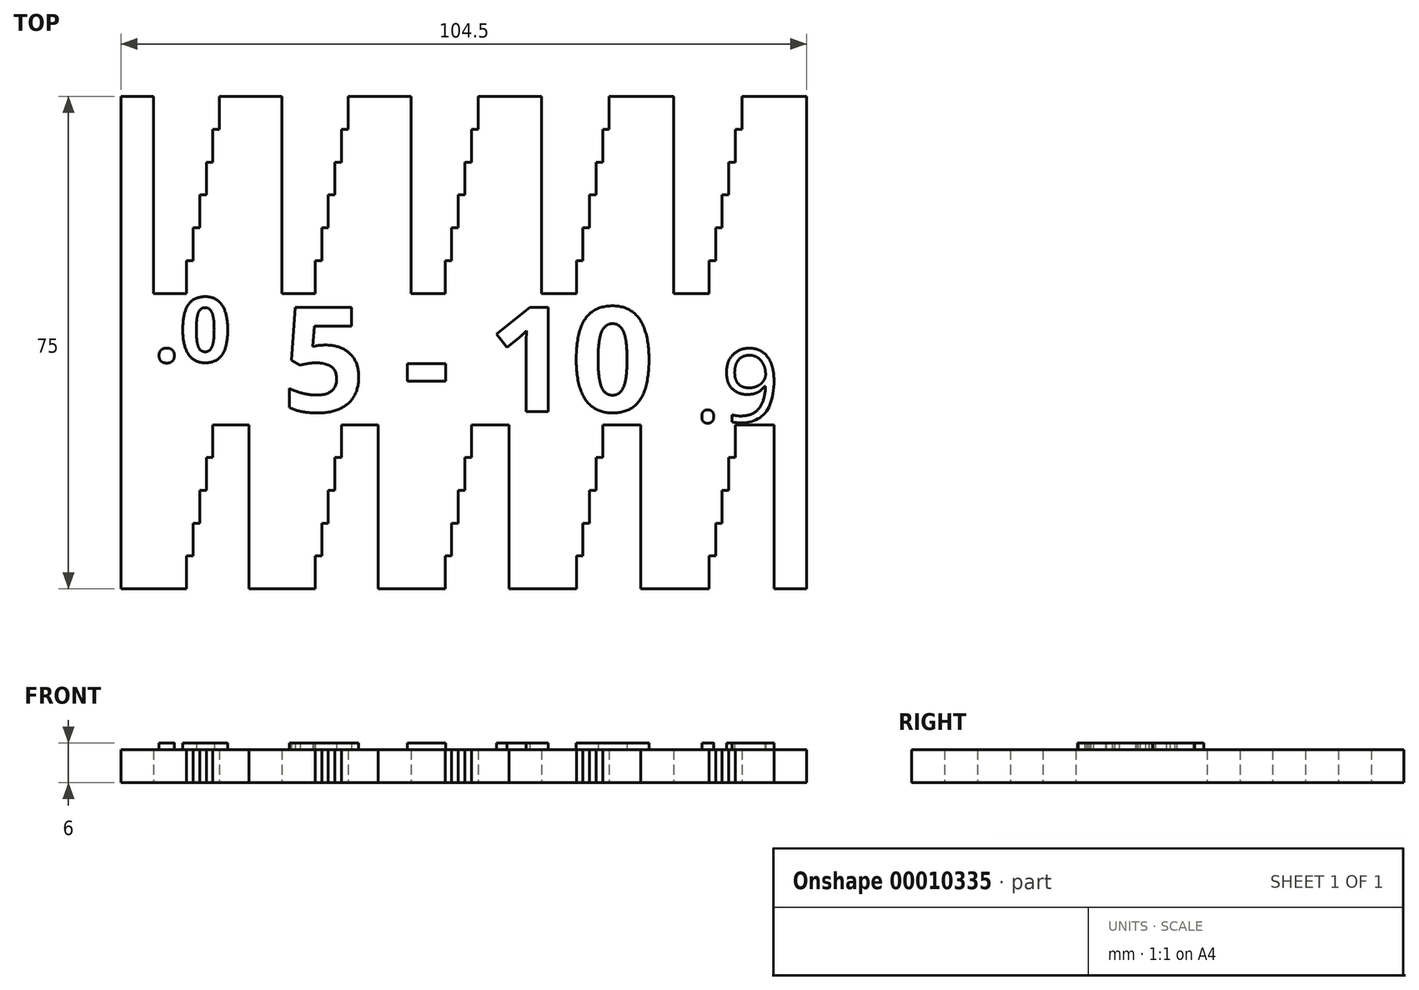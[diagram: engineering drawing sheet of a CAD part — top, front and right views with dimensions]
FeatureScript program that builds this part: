
annotation { "Feature Type Name" : "Feature", "Feature Type Description" : "" }
export const myFeature = defineFeature(function(context is Context, id is Id, definition is map)
    precondition{}
    {
        {
            var Q0;
            Q0=qCreatedBy(makeId("Top.planeOp"),FACE);
            var sketch = newSketch(context, id + "F0", { "sketchPlane" : qUnion([Q0])});
            skLineSegment(sketch, "E0.bottom", {"start": v(-54.67, 33.99) * mm, "end": v(49.83, 33.99) * mm, "construction": true});
            skLineSegment(sketch, "E0.top", {"start": v(-54.67, -41.01) * mm, "end": v(49.83, -41.01) * mm, "construction": true});
            skLineSegment(sketch, "E0.left", {"start": v(-54.67, 33.99) * mm, "end": v(-54.67, -41.01) * mm, "construction": true});
            skLineSegment(sketch, "E0.right", {"start": v(49.83, 33.99) * mm, "end": v(49.83, -41.01) * mm, "construction": true});
            skLineSegment(sketch, "E1.bottom", {"start": v(-54.67, 33.99) * mm, "end": v(-49.67, 33.99) * mm});
            skLineSegment(sketch, "E1.top", {"start": v(-54.67, -41.01) * mm, "end": v(-49.67, -41.01) * mm});
            skLineSegment(sketch, "E1.left", {"start": v(-54.67, 33.99) * mm, "end": v(-54.67, -41.01) * mm});
            skLineSegment(sketch, "E1.right", {"start": v(-49.67, 33.99) * mm, "end": v(-49.67, -41.01) * mm});
            skLineSegment(sketch, "E2.bottom", {"start": v(-49.67, 3.99) * mm, "end": v(-44.67, 3.99) * mm});
            skLineSegment(sketch, "E2.top", {"start": v(-49.67, -41.01) * mm, "end": v(-44.67, -41.01) * mm});
            skLineSegment(sketch, "E2.left", {"start": v(-49.67, 3.99) * mm, "end": v(-49.67, -41.01) * mm});
            skLineSegment(sketch, "E2.right", {"start": v(-44.67, 3.99) * mm, "end": v(-44.67, -41.01) * mm});
            skLineSegment(sketch, "E3.bottom", {"start": v(-44.67, -36.01) * mm, "end": v(-43.67, -36.01) * mm});
            skLineSegment(sketch, "E3.top", {"start": v(-44.67, 8.99) * mm, "end": v(-43.67, 8.99) * mm});
            skLineSegment(sketch, "E3.left", {"start": v(-44.67, -36.01) * mm, "end": v(-44.67, 8.99) * mm});
            skLineSegment(sketch, "E3.right", {"start": v(-43.67, -36.01) * mm, "end": v(-43.67, 8.99) * mm});
            skLineSegment(sketch, "E4.bottom", {"start": v(-43.67, -31.01) * mm, "end": v(-42.67, -31.01) * mm});
            skLineSegment(sketch, "E4.top", {"start": v(-43.67, 13.99) * mm, "end": v(-42.67, 13.99) * mm});
            skLineSegment(sketch, "E4.left", {"start": v(-43.67, -31.01) * mm, "end": v(-43.67, 13.99) * mm});
            skLineSegment(sketch, "E4.right", {"start": v(-42.67, -31.01) * mm, "end": v(-42.67, 13.99) * mm});
            skLineSegment(sketch, "E5.bottom", {"start": v(-42.67, -26.01) * mm, "end": v(-41.67, -26.01) * mm});
            skLineSegment(sketch, "E5.top", {"start": v(-42.67, 18.99) * mm, "end": v(-41.67, 18.99) * mm});
            skLineSegment(sketch, "E5.left", {"start": v(-42.67, -26.01) * mm, "end": v(-42.67, 18.99) * mm});
            skLineSegment(sketch, "E5.right", {"start": v(-41.67, -26.01) * mm, "end": v(-41.67, 18.99) * mm});
            skLineSegment(sketch, "E6.bottom", {"start": v(-41.67, -21.01) * mm, "end": v(-40.67, -21.01) * mm});
            skLineSegment(sketch, "E6.top", {"start": v(-41.67, 23.99) * mm, "end": v(-40.67, 23.99) * mm});
            skLineSegment(sketch, "E6.left", {"start": v(-41.67, -21.01) * mm, "end": v(-41.67, 23.99) * mm});
            skLineSegment(sketch, "E6.right", {"start": v(-40.67, -21.01) * mm, "end": v(-40.67, 23.99) * mm});
            skLineSegment(sketch, "E7.bottom", {"start": v(-40.67, -16.01) * mm, "end": v(-39.67, -16.01) * mm});
            skLineSegment(sketch, "E7.top", {"start": v(-40.67, 28.99) * mm, "end": v(-39.67, 28.99) * mm});
            skLineSegment(sketch, "E7.left", {"start": v(-40.67, -16.01) * mm, "end": v(-40.67, 28.99) * mm});
            skLineSegment(sketch, "E7.right", {"start": v(-39.67, -16.01) * mm, "end": v(-39.67, 28.99) * mm});
            skLineSegment(sketch, "E8.bottom", {"start": v(-39.67, -16.01) * mm, "end": v(-35.17, -16.01) * mm});
            skLineSegment(sketch, "E8.top", {"start": v(-39.67, 33.99) * mm, "end": v(-35.17, 33.99) * mm});
            skLineSegment(sketch, "E8.left", {"start": v(-39.67, -16.01) * mm, "end": v(-39.67, 33.99) * mm});
            skLineSegment(sketch, "E8.right", {"start": v(-35.17, -16.01) * mm, "end": v(-35.17, 33.99) * mm});
            skLineSegment(sketch, "E9.right", {"start": v(-22.07, -26.01) * mm, "end": v(-22.07, 18.99) * mm});
            skLineSegment(sketch, "E10.right", {"start": v(-20.07, -16.01) * mm, "end": v(-20.07, 28.99) * mm});
            skLineSegment(sketch, "E11.left", {"start": v(-20.07, -16.01) * mm, "end": v(-20.07, 33.99) * mm});
            skLineSegment(sketch, "E12.left", {"start": v(-30.17, 3.99) * mm, "end": v(-30.17, -41.01) * mm});
            skLineSegment(sketch, "E12.right", {"start": v(-25.07, 3.99) * mm, "end": v(-25.07, -41.01) * mm});
            skLineSegment(sketch, "E13.right", {"start": v(-21.07, -21.01) * mm, "end": v(-21.07, 23.99) * mm});
            skLineSegment(sketch, "E11.right", {"start": v(-15.47, -16.01) * mm, "end": v(-15.47, 33.99) * mm});
            skLineSegment(sketch, "E14.right", {"start": v(-23.07, -31.01) * mm, "end": v(-23.07, 13.99) * mm});
            skLineSegment(sketch, "E13.left", {"start": v(-22.07, -21.01) * mm, "end": v(-22.07, 23.99) * mm});
            skLineSegment(sketch, "E11.bottom", {"start": v(-20.07, -16.01) * mm, "end": v(-15.47, -16.01) * mm});
            skLineSegment(sketch, "E9.left", {"start": v(-23.07, -26.01) * mm, "end": v(-23.07, 18.99) * mm});
            skLineSegment(sketch, "E10.left", {"start": v(-21.07, -16.01) * mm, "end": v(-21.07, 28.99) * mm});
            skLineSegment(sketch, "E15.bottom", {"start": v(-35.17, 33.99) * mm, "end": v(-30.17, 33.99) * mm});
            skLineSegment(sketch, "E15.left", {"start": v(-35.17, 33.99) * mm, "end": v(-35.17, -41.01) * mm});
            skLineSegment(sketch, "E15.top", {"start": v(-35.17, -41.01) * mm, "end": v(-30.17, -41.01) * mm});
            skLineSegment(sketch, "E12.bottom", {"start": v(-30.17, 3.99) * mm, "end": v(-25.07, 3.99) * mm});
            skLineSegment(sketch, "E15.right", {"start": v(-30.17, 33.99) * mm, "end": v(-30.17, -41.01) * mm});
            skLineSegment(sketch, "E12.top", {"start": v(-30.17, -41.01) * mm, "end": v(-25.07, -41.01) * mm});
            skLineSegment(sketch, "E16.left", {"start": v(-25.07, -36.01) * mm, "end": v(-25.07, 8.99) * mm});
            skLineSegment(sketch, "E14.left", {"start": v(-24.07, -31.01) * mm, "end": v(-24.07, 13.99) * mm});
            skLineSegment(sketch, "E16.right", {"start": v(-24.07, -36.01) * mm, "end": v(-24.07, 8.99) * mm});
            skLineSegment(sketch, "E11.top", {"start": v(-20.07, 33.99) * mm, "end": v(-15.47, 33.99) * mm});
            skLineSegment(sketch, "E16.top", {"start": v(-25.07, 8.99) * mm, "end": v(-24.07, 8.99) * mm});
            skLineSegment(sketch, "E14.bottom", {"start": v(-24.07, -31.01) * mm, "end": v(-23.07, -31.01) * mm});
            skLineSegment(sketch, "E10.bottom", {"start": v(-21.07, -16.01) * mm, "end": v(-20.07, -16.01) * mm});
            skLineSegment(sketch, "E13.top", {"start": v(-22.07, 23.99) * mm, "end": v(-21.07, 23.99) * mm});
            skLineSegment(sketch, "E17.left", {"start": v(-35.59, 33.94) * mm, "end": v(-35.59, -41.06) * mm, "construction": true});
            skLineSegment(sketch, "E14.top", {"start": v(-24.07, 13.99) * mm, "end": v(-23.07, 13.99) * mm});
            skLineSegment(sketch, "E9.top", {"start": v(-23.07, 18.99) * mm, "end": v(-22.07, 18.99) * mm});
            skLineSegment(sketch, "E9.bottom", {"start": v(-23.07, -26.01) * mm, "end": v(-22.07, -26.01) * mm});
            skLineSegment(sketch, "E10.top", {"start": v(-21.07, 28.99) * mm, "end": v(-20.07, 28.99) * mm});
            skLineSegment(sketch, "E16.bottom", {"start": v(-25.07, -36.01) * mm, "end": v(-24.07, -36.01) * mm});
            skLineSegment(sketch, "E13.bottom", {"start": v(-22.07, -21.01) * mm, "end": v(-21.07, -21.01) * mm});
            skLineSegment(sketch, "E18.right", {"start": v(-2.27, -26.01) * mm, "end": v(-2.27, 18.99) * mm});
            skLineSegment(sketch, "E19.right", {"start": v(-0.27, -16.01) * mm, "end": v(-0.27, 28.99) * mm});
            skLineSegment(sketch, "E20.left", {"start": v(-0.27, -16.01) * mm, "end": v(-0.27, 33.99) * mm});
            skLineSegment(sketch, "E21.left", {"start": v(-10.47, 3.99) * mm, "end": v(-10.47, -41.01) * mm});
            skLineSegment(sketch, "E21.right", {"start": v(-5.27, 3.99) * mm, "end": v(-5.27, -41.01) * mm});
            skLineSegment(sketch, "E22.right", {"start": v(-1.27, -21.01) * mm, "end": v(-1.27, 23.99) * mm});
            skLineSegment(sketch, "E20.right", {"start": v(4.43, -16.01) * mm, "end": v(4.43, 33.99) * mm});
            skLineSegment(sketch, "E23.right", {"start": v(-3.27, -31.01) * mm, "end": v(-3.27, 13.99) * mm});
            skLineSegment(sketch, "E22.left", {"start": v(-2.27, -21.01) * mm, "end": v(-2.27, 23.99) * mm});
            skLineSegment(sketch, "E20.bottom", {"start": v(-0.27, -16.01) * mm, "end": v(4.43, -16.01) * mm});
            skLineSegment(sketch, "E18.left", {"start": v(-3.27, -26.01) * mm, "end": v(-3.27, 18.99) * mm});
            skLineSegment(sketch, "E19.left", {"start": v(-1.27, -16.01) * mm, "end": v(-1.27, 28.99) * mm});
            skLineSegment(sketch, "E24.bottom", {"start": v(-15.47, 33.99) * mm, "end": v(-10.47, 33.99) * mm});
            skLineSegment(sketch, "E24.left", {"start": v(-15.47, 33.99) * mm, "end": v(-15.47, -41.01) * mm});
            skLineSegment(sketch, "E24.top", {"start": v(-15.47, -41.01) * mm, "end": v(-10.47, -41.01) * mm});
            skLineSegment(sketch, "E21.bottom", {"start": v(-10.47, 3.99) * mm, "end": v(-5.27, 3.99) * mm});
            skLineSegment(sketch, "E24.right", {"start": v(-10.47, 33.99) * mm, "end": v(-10.47, -41.01) * mm});
            skLineSegment(sketch, "E21.top", {"start": v(-10.47, -41.01) * mm, "end": v(-5.27, -41.01) * mm});
            skLineSegment(sketch, "E25.left", {"start": v(-5.27, -36.01) * mm, "end": v(-5.27, 8.99) * mm});
            skLineSegment(sketch, "E23.left", {"start": v(-4.27, -31.01) * mm, "end": v(-4.27, 13.99) * mm});
            skLineSegment(sketch, "E25.right", {"start": v(-4.27, -36.01) * mm, "end": v(-4.27, 8.99) * mm});
            skLineSegment(sketch, "E20.top", {"start": v(-0.27, 33.99) * mm, "end": v(4.43, 33.99) * mm});
            skLineSegment(sketch, "E25.top", {"start": v(-5.27, 8.99) * mm, "end": v(-4.27, 8.99) * mm});
            skLineSegment(sketch, "E23.bottom", {"start": v(-4.27, -31.01) * mm, "end": v(-3.27, -31.01) * mm});
            skLineSegment(sketch, "E19.bottom", {"start": v(-1.27, -16.01) * mm, "end": v(-0.27, -16.01) * mm});
            skLineSegment(sketch, "E22.top", {"start": v(-2.27, 23.99) * mm, "end": v(-1.27, 23.99) * mm});
            skLineSegment(sketch, "E23.top", {"start": v(-4.27, 13.99) * mm, "end": v(-3.27, 13.99) * mm});
            skLineSegment(sketch, "E18.top", {"start": v(-3.27, 18.99) * mm, "end": v(-2.27, 18.99) * mm});
            skLineSegment(sketch, "E18.bottom", {"start": v(-3.27, -26.01) * mm, "end": v(-2.27, -26.01) * mm});
            skLineSegment(sketch, "E19.top", {"start": v(-1.27, 28.99) * mm, "end": v(-0.27, 28.99) * mm});
            skLineSegment(sketch, "E25.bottom", {"start": v(-5.27, -36.01) * mm, "end": v(-4.27, -36.01) * mm});
            skLineSegment(sketch, "E22.bottom", {"start": v(-2.27, -21.01) * mm, "end": v(-1.27, -21.01) * mm});
            skLineSegment(sketch, "E26.left", {"start": v(15.73, -31.01) * mm, "end": v(15.73, 13.99) * mm});
            skLineSegment(sketch, "E27.right", {"start": v(37.93, -26.01) * mm, "end": v(37.93, 18.99) * mm});
            skLineSegment(sketch, "E28.right", {"start": v(35.93, -36.01) * mm, "end": v(35.93, 8.99) * mm});
            skLineSegment(sketch, "E29.bottom", {"start": v(19.73, -16.01) * mm, "end": v(24.53, -16.01) * mm});
            skLineSegment(sketch, "E30.bottom", {"start": v(24.53, 33.99) * mm, "end": v(29.53, 33.99) * mm});
            skLineSegment(sketch, "E30.right", {"start": v(29.53, 33.99) * mm, "end": v(29.53, -41.01) * mm});
            skLineSegment(sketch, "E31.right", {"start": v(34.93, 3.99) * mm, "end": v(34.93, -41.01) * mm});
            skLineSegment(sketch, "E32.right", {"start": v(49.83, 33.99) * mm, "end": v(49.83, -41.01) * mm});
            skLineSegment(sketch, "E33.left", {"start": v(39.93, -16.01) * mm, "end": v(39.93, 33.99) * mm});
            skLineSegment(sketch, "E33.top", {"start": v(39.93, 33.99) * mm, "end": v(44.83, 33.99) * mm});
            skLineSegment(sketch, "E28.left", {"start": v(34.93, -36.01) * mm, "end": v(34.93, 8.99) * mm});
            skLineSegment(sketch, "E34.right", {"start": v(38.93, -21.01) * mm, "end": v(38.93, 23.99) * mm});
            skLineSegment(sketch, "E35.left", {"start": v(16.73, -26.01) * mm, "end": v(16.73, 18.99) * mm});
            skLineSegment(sketch, "E36.top", {"start": v(38.93, 28.99) * mm, "end": v(39.93, 28.99) * mm});
            skLineSegment(sketch, "E31.left", {"start": v(29.53, 3.99) * mm, "end": v(29.53, -41.01) * mm});
            skLineSegment(sketch, "E35.right", {"start": v(17.73, -26.01) * mm, "end": v(17.73, 18.99) * mm});
            skLineSegment(sketch, "E32.left", {"start": v(44.83, 33.99) * mm, "end": v(44.83, -41.01) * mm});
            skLineSegment(sketch, "E29.left", {"start": v(19.73, -16.01) * mm, "end": v(19.73, 33.99) * mm});
            skLineSegment(sketch, "E37.right", {"start": v(14.73, 3.99) * mm, "end": v(14.73, -41.01) * mm});
            skLineSegment(sketch, "E38.left", {"start": v(35.93, -31.01) * mm, "end": v(35.93, 13.99) * mm});
            skLineSegment(sketch, "E39.bottom", {"start": v(17.73, -21.01) * mm, "end": v(18.73, -21.01) * mm});
            skLineSegment(sketch, "E40.top", {"start": v(18.73, 28.99) * mm, "end": v(19.73, 28.99) * mm});
            skLineSegment(sketch, "E33.bottom", {"start": v(39.93, -16.01) * mm, "end": v(44.83, -16.01) * mm});
            skLineSegment(sketch, "E30.top", {"start": v(24.53, -41.01) * mm, "end": v(29.53, -41.01) * mm});
            skLineSegment(sketch, "E39.left", {"start": v(17.73, -21.01) * mm, "end": v(17.73, 23.99) * mm});
            skLineSegment(sketch, "E28.top", {"start": v(34.93, 8.99) * mm, "end": v(35.93, 8.99) * mm});
            skLineSegment(sketch, "E40.left", {"start": v(18.73, -16.01) * mm, "end": v(18.73, 28.99) * mm});
            skLineSegment(sketch, "E33.right", {"start": v(44.83, -16.01) * mm, "end": v(44.83, 33.99) * mm});
            skLineSegment(sketch, "E27.left", {"start": v(36.93, -26.01) * mm, "end": v(36.93, 18.99) * mm});
            skLineSegment(sketch, "E41.right", {"start": v(15.73, -36.01) * mm, "end": v(15.73, 8.99) * mm});
            skLineSegment(sketch, "E31.top", {"start": v(29.53, -41.01) * mm, "end": v(34.93, -41.01) * mm});
            skLineSegment(sketch, "E36.right", {"start": v(39.93, -16.01) * mm, "end": v(39.93, 28.99) * mm});
            skLineSegment(sketch, "E41.left", {"start": v(14.73, -36.01) * mm, "end": v(14.73, 8.99) * mm});
            skLineSegment(sketch, "E34.left", {"start": v(37.93, -21.01) * mm, "end": v(37.93, 23.99) * mm});
            skLineSegment(sketch, "E40.right", {"start": v(19.73, -16.01) * mm, "end": v(19.73, 28.99) * mm});
            skLineSegment(sketch, "E36.left", {"start": v(38.93, -16.01) * mm, "end": v(38.93, 28.99) * mm});
            skLineSegment(sketch, "E39.right", {"start": v(18.73, -21.01) * mm, "end": v(18.73, 23.99) * mm});
            skLineSegment(sketch, "E38.right", {"start": v(36.93, -31.01) * mm, "end": v(36.93, 13.99) * mm});
            skLineSegment(sketch, "E26.right", {"start": v(16.73, -31.01) * mm, "end": v(16.73, 13.99) * mm});
            skLineSegment(sketch, "E29.right", {"start": v(24.53, -16.01) * mm, "end": v(24.53, 33.99) * mm});
            skLineSegment(sketch, "E32.top", {"start": v(44.83, -41.01) * mm, "end": v(49.83, -41.01) * mm});
            skLineSegment(sketch, "E31.bottom", {"start": v(29.53, 3.99) * mm, "end": v(34.93, 3.99) * mm});
            skLineSegment(sketch, "E42.bottom", {"start": v(4.43, 33.99) * mm, "end": v(9.43, 33.99) * mm});
            skLineSegment(sketch, "E42.left", {"start": v(4.43, 33.99) * mm, "end": v(4.43, -41.01) * mm});
            skLineSegment(sketch, "E42.top", {"start": v(4.43, -41.01) * mm, "end": v(9.43, -41.01) * mm});
            skLineSegment(sketch, "E37.bottom", {"start": v(9.43, 3.99) * mm, "end": v(14.73, 3.99) * mm});
            skLineSegment(sketch, "E42.right", {"start": v(9.43, 33.99) * mm, "end": v(9.43, -41.01) * mm});
            skLineSegment(sketch, "E37.left", {"start": v(9.43, 3.99) * mm, "end": v(9.43, -41.01) * mm});
            skLineSegment(sketch, "E29.top", {"start": v(19.73, 33.99) * mm, "end": v(24.53, 33.99) * mm});
            skLineSegment(sketch, "E30.left", {"start": v(24.53, 33.99) * mm, "end": v(24.53, -41.01) * mm});
            skLineSegment(sketch, "E34.top", {"start": v(37.93, 23.99) * mm, "end": v(38.93, 23.99) * mm});
            skLineSegment(sketch, "E37.top", {"start": v(9.43, -41.01) * mm, "end": v(14.73, -41.01) * mm});
            skLineSegment(sketch, "E27.bottom", {"start": v(36.93, -26.01) * mm, "end": v(37.93, -26.01) * mm});
            skLineSegment(sketch, "E32.bottom", {"start": v(44.83, 33.99) * mm, "end": v(49.83, 33.99) * mm});
            skLineSegment(sketch, "E41.bottom", {"start": v(14.73, -36.01) * mm, "end": v(15.73, -36.01) * mm});
            skLineSegment(sketch, "E34.bottom", {"start": v(37.93, -21.01) * mm, "end": v(38.93, -21.01) * mm});
            skLineSegment(sketch, "E27.top", {"start": v(36.93, 18.99) * mm, "end": v(37.93, 18.99) * mm});
            skLineSegment(sketch, "E38.top", {"start": v(35.93, 13.99) * mm, "end": v(36.93, 13.99) * mm});
            skLineSegment(sketch, "E39.top", {"start": v(17.73, 23.99) * mm, "end": v(18.73, 23.99) * mm});
            skLineSegment(sketch, "E41.top", {"start": v(14.73, 8.99) * mm, "end": v(15.73, 8.99) * mm});
            skLineSegment(sketch, "E35.top", {"start": v(16.73, 18.99) * mm, "end": v(17.73, 18.99) * mm});
            skLineSegment(sketch, "E26.top", {"start": v(15.73, 13.99) * mm, "end": v(16.73, 13.99) * mm});
            skLineSegment(sketch, "E26.bottom", {"start": v(15.73, -31.01) * mm, "end": v(16.73, -31.01) * mm});
            skLineSegment(sketch, "E35.bottom", {"start": v(16.73, -26.01) * mm, "end": v(17.73, -26.01) * mm});
            skLineSegment(sketch, "E36.bottom", {"start": v(38.93, -16.01) * mm, "end": v(39.93, -16.01) * mm});
            skLineSegment(sketch, "E40.bottom", {"start": v(18.73, -16.01) * mm, "end": v(19.73, -16.01) * mm});
            skLineSegment(sketch, "E38.bottom", {"start": v(35.93, -31.01) * mm, "end": v(36.93, -31.01) * mm});
            skLineSegment(sketch, "E28.bottom", {"start": v(34.93, -36.01) * mm, "end": v(35.93, -36.01) * mm});
            skSolve(sketch);
        }
        {
            var Q0;
            Q0 = qSketchRegion(id + "F0", true);
            extrude(context, id + "F1", {"entities" : qUnion([Q0]), "depth" : 5 * mm});
        }
        {
            var Q0;
            Q0=makeQuery(id+"F1.opExtrude","CAP_FACE",FACE,{"disambiguationData":[OSD([sQuery(id+"F0.wireOp",EDGE,"E1.bottom"),sQuery(id+"F0.wireOp",EDGE,"E1.top"),sQuery(id+"F0.wireOp",EDGE,"E1.left"),sQuery(id+"F0.wireOp",EDGE,"E1.right"),sQuery(id+"F0.wireOp",EDGE,"E2.bottom"),sQuery(id+"F0.wireOp",EDGE,"E2.top"),sQuery(id+"F0.wireOp",EDGE,"E2.right"),sQuery(id+"F0.wireOp",EDGE,"E3.bottom"),sQuery(id+"F0.wireOp",EDGE,"E3.top"),sQuery(id+"F0.wireOp",EDGE,"E3.left"),sQuery(id+"F0.wireOp",EDGE,"E3.right"),sQuery(id+"F0.wireOp",EDGE,"E4.bottom"),sQuery(id+"F0.wireOp",EDGE,"E4.top"),sQuery(id+"F0.wireOp",EDGE,"E4.left"),sQuery(id+"F0.wireOp",EDGE,"E4.right"),sQuery(id+"F0.wireOp",EDGE,"E5.bottom"),sQuery(id+"F0.wireOp",EDGE,"E5.top"),sQuery(id+"F0.wireOp",EDGE,"E5.left"),sQuery(id+"F0.wireOp",EDGE,"E5.right"),sQuery(id+"F0.wireOp",EDGE,"E6.bottom"),sQuery(id+"F0.wireOp",EDGE,"E6.top"),sQuery(id+"F0.wireOp",EDGE,"E6.left"),sQuery(id+"F0.wireOp",EDGE,"E6.right"),sQuery(id+"F0.wireOp",EDGE,"E7.bottom"),sQuery(id+"F0.wireOp",EDGE,"E7.top"),sQuery(id+"F0.wireOp",EDGE,"E7.left"),sQuery(id+"F0.wireOp",EDGE,"E8.bottom"),sQuery(id+"F0.wireOp",EDGE,"E8.top"),sQuery(id+"F0.wireOp",EDGE,"E8.left"),sQuery(id+"F0.wireOp",EDGE,"E9.right"),sQuery(id+"F0.wireOp",EDGE,"E11.left"),sQuery(id+"F0.wireOp",EDGE,"E12.right"),sQuery(id+"F0.wireOp",EDGE,"E13.right"),sQuery(id+"F0.wireOp",EDGE,"E14.right"),sQuery(id+"F0.wireOp",EDGE,"E13.left"),sQuery(id+"F0.wireOp",EDGE,"E11.bottom"),sQuery(id+"F0.wireOp",EDGE,"E9.left"),sQuery(id+"F0.wireOp",EDGE,"E10.left"),sQuery(id+"F0.wireOp",EDGE,"E15.bottom"),sQuery(id+"F0.wireOp",EDGE,"E15.left"),sQuery(id+"F0.wireOp",EDGE,"E15.top"),sQuery(id+"F0.wireOp",EDGE,"E12.bottom"),sQuery(id+"F0.wireOp",EDGE,"E15.right"),sQuery(id+"F0.wireOp",EDGE,"E12.top"),sQuery(id+"F0.wireOp",EDGE,"E16.left"),sQuery(id+"F0.wireOp",EDGE,"E14.left"),sQuery(id+"F0.wireOp",EDGE,"E16.right"),sQuery(id+"F0.wireOp",EDGE,"E11.top"),sQuery(id+"F0.wireOp",EDGE,"E16.top"),sQuery(id+"F0.wireOp",EDGE,"E14.bottom"),sQuery(id+"F0.wireOp",EDGE,"E10.bottom"),sQuery(id+"F0.wireOp",EDGE,"E13.top"),sQuery(id+"F0.wireOp",EDGE,"E14.top"),sQuery(id+"F0.wireOp",EDGE,"E9.top"),sQuery(id+"F0.wireOp",EDGE,"E9.bottom"),sQuery(id+"F0.wireOp",EDGE,"E10.top"),sQuery(id+"F0.wireOp",EDGE,"E16.bottom"),sQuery(id+"F0.wireOp",EDGE,"E13.bottom"),sQuery(id+"F0.wireOp",EDGE,"E18.right"),sQuery(id+"F0.wireOp",EDGE,"E20.left"),sQuery(id+"F0.wireOp",EDGE,"E21.right"),sQuery(id+"F0.wireOp",EDGE,"E22.right"),sQuery(id+"F0.wireOp",EDGE,"E23.right"),sQuery(id+"F0.wireOp",EDGE,"E22.left"),sQuery(id+"F0.wireOp",EDGE,"E20.bottom"),sQuery(id+"F0.wireOp",EDGE,"E18.left"),sQuery(id+"F0.wireOp",EDGE,"E19.left"),sQuery(id+"F0.wireOp",EDGE,"E24.bottom"),sQuery(id+"F0.wireOp",EDGE,"E24.left"),sQuery(id+"F0.wireOp",EDGE,"E24.top"),sQuery(id+"F0.wireOp",EDGE,"E21.bottom"),sQuery(id+"F0.wireOp",EDGE,"E24.right"),sQuery(id+"F0.wireOp",EDGE,"E21.top"),sQuery(id+"F0.wireOp",EDGE,"E25.left"),sQuery(id+"F0.wireOp",EDGE,"E23.left"),sQuery(id+"F0.wireOp",EDGE,"E25.right"),sQuery(id+"F0.wireOp",EDGE,"E20.top"),sQuery(id+"F0.wireOp",EDGE,"E25.top"),sQuery(id+"F0.wireOp",EDGE,"E23.bottom"),sQuery(id+"F0.wireOp",EDGE,"E19.bottom"),sQuery(id+"F0.wireOp",EDGE,"E22.top"),sQuery(id+"F0.wireOp",EDGE,"E23.top"),sQuery(id+"F0.wireOp",EDGE,"E18.top"),sQuery(id+"F0.wireOp",EDGE,"E18.bottom"),sQuery(id+"F0.wireOp",EDGE,"E19.top"),sQuery(id+"F0.wireOp",EDGE,"E25.bottom"),sQuery(id+"F0.wireOp",EDGE,"E22.bottom"),sQuery(id+"F0.wireOp",EDGE,"E26.left"),sQuery(id+"F0.wireOp",EDGE,"E27.right"),sQuery(id+"F0.wireOp",EDGE,"E28.right"),sQuery(id+"F0.wireOp",EDGE,"E29.bottom"),sQuery(id+"F0.wireOp",EDGE,"E30.bottom"),sQuery(id+"F0.wireOp",EDGE,"E30.right"),sQuery(id+"F0.wireOp",EDGE,"E31.right"),sQuery(id+"F0.wireOp",EDGE,"E32.right"),sQuery(id+"F0.wireOp",EDGE,"E33.left"),sQuery(id+"F0.wireOp",EDGE,"E33.top"),sQuery(id+"F0.wireOp",EDGE,"E28.left"),sQuery(id+"F0.wireOp",EDGE,"E34.right"),sQuery(id+"F0.wireOp",EDGE,"E35.left"),sQuery(id+"F0.wireOp",EDGE,"E36.top"),sQuery(id+"F0.wireOp",EDGE,"E35.right"),sQuery(id+"F0.wireOp",EDGE,"E32.left"),sQuery(id+"F0.wireOp",EDGE,"E29.left"),sQuery(id+"F0.wireOp",EDGE,"E37.right"),sQuery(id+"F0.wireOp",EDGE,"E38.left"),sQuery(id+"F0.wireOp",EDGE,"E39.bottom"),sQuery(id+"F0.wireOp",EDGE,"E40.top"),sQuery(id+"F0.wireOp",EDGE,"E33.bottom"),sQuery(id+"F0.wireOp",EDGE,"E30.top"),sQuery(id+"F0.wireOp",EDGE,"E39.left"),sQuery(id+"F0.wireOp",EDGE,"E28.top"),sQuery(id+"F0.wireOp",EDGE,"E40.left"),sQuery(id+"F0.wireOp",EDGE,"E27.left"),sQuery(id+"F0.wireOp",EDGE,"E41.right"),sQuery(id+"F0.wireOp",EDGE,"E31.top"),sQuery(id+"F0.wireOp",EDGE,"E41.left"),sQuery(id+"F0.wireOp",EDGE,"E34.left"),sQuery(id+"F0.wireOp",EDGE,"E36.left"),sQuery(id+"F0.wireOp",EDGE,"E39.right"),sQuery(id+"F0.wireOp",EDGE,"E38.right"),sQuery(id+"F0.wireOp",EDGE,"E26.right"),sQuery(id+"F0.wireOp",EDGE,"E32.top"),sQuery(id+"F0.wireOp",EDGE,"E31.bottom"),sQuery(id+"F0.wireOp",EDGE,"E42.bottom"),sQuery(id+"F0.wireOp",EDGE,"E42.left"),sQuery(id+"F0.wireOp",EDGE,"E42.top"),sQuery(id+"F0.wireOp",EDGE,"E37.bottom"),sQuery(id+"F0.wireOp",EDGE,"E42.right"),sQuery(id+"F0.wireOp",EDGE,"E29.top"),sQuery(id+"F0.wireOp",EDGE,"E30.left"),sQuery(id+"F0.wireOp",EDGE,"E34.top"),sQuery(id+"F0.wireOp",EDGE,"E37.top"),sQuery(id+"F0.wireOp",EDGE,"E27.bottom"),sQuery(id+"F0.wireOp",EDGE,"E32.bottom"),sQuery(id+"F0.wireOp",EDGE,"E41.bottom"),sQuery(id+"F0.wireOp",EDGE,"E34.bottom"),sQuery(id+"F0.wireOp",EDGE,"E27.top"),sQuery(id+"F0.wireOp",EDGE,"E38.top"),sQuery(id+"F0.wireOp",EDGE,"E39.top"),sQuery(id+"F0.wireOp",EDGE,"E41.top"),sQuery(id+"F0.wireOp",EDGE,"E35.top"),sQuery(id+"F0.wireOp",EDGE,"E26.top"),sQuery(id+"F0.wireOp",EDGE,"E26.bottom"),sQuery(id+"F0.wireOp",EDGE,"E35.bottom"),sQuery(id+"F0.wireOp",EDGE,"E36.bottom"),sQuery(id+"F0.wireOp",EDGE,"E40.bottom"),sQuery(id+"F0.wireOp",EDGE,"E38.bottom"),sQuery(id+"F0.wireOp",EDGE,"E28.bottom")])],"isStart":false});
            var sketch = newSketch(context, id + "F2", { "sketchPlane" : qUnion([Q0])});
            skText(sketch, "E43", { "text": "5 - 10", "fontName": "OpenSans-Bold.ttf"});
            skText(sketch, "E44", { "text": ".0", "fontName": "OpenSans-Bold.ttf"});
            skText(sketch, "E45", { "text": ".9", "fontName": "OpenSans-Regular.ttf"});
            const initialGuessF2  = {"E43": [-0.03011, -0.014, 1, 0, 0.01598], "E44": [-0.04965, -0.00644, 1, 0, 0.00987], "E45": [0.03268, -0.01557, 1, 0, 0.01115]};
            skSetInitialGuess(sketch, initialGuessF2);
            skSolve(sketch);
        }
        {
            var Q0;
            Q0=makeQuery(id+"F2.imprint","IMPRINT",FACE,{"disambiguationData":[TD([[makeQuery(id+"F2.imprint","IMPRINT",EDGE,{"derivedFrom":sQuery(id+"F2.wireOp",EDGE,"E43.sketch_text.stroke-0")}),-1.0]])]});
            var Q1;
            Q1=makeQuery(id+"F2.imprint","IMPRINT",FACE,{"disambiguationData":[TD([[makeQuery(id+"F2.imprint","IMPRINT",EDGE,{"derivedFrom":sQuery(id+"F2.wireOp",EDGE,"E43.sketch_text.stroke-20")}),-1.0]])]});
            var Q2;
            Q2=makeQuery(id+"F2.imprint","IMPRINT",FACE,{"disambiguationData":[TD([[makeQuery(id+"F2.imprint","IMPRINT",EDGE,{"derivedFrom":sQuery(id+"F2.wireOp",EDGE,"E43.sketch_text.stroke-24")}),-1.0]])]});
            var Q3;
            Q3=makeQuery(id+"F2.imprint","IMPRINT",FACE,{"disambiguationData":[TD([[makeQuery(id+"F2.imprint","IMPRINT",EDGE,{"derivedFrom":sQuery(id+"F2.wireOp",EDGE,"E43.sketch_text.stroke-34")}),-1.0]])]});
            var Q4;
            Q4=makeQuery(id+"F2.imprint","IMPRINT",FACE,{"disambiguationData":[TD([[makeQuery(id+"F2.imprint","IMPRINT",EDGE,{"derivedFrom":sQuery(id+"F2.wireOp",EDGE,"E44.sketch_text.stroke-8")}),-1.0]])]});
            var Q5;
            Q5=makeQuery(id+"F2.imprint","IMPRINT",FACE,{"disambiguationData":[TD([[makeQuery(id+"F2.imprint","IMPRINT",EDGE,{"derivedFrom":sQuery(id+"F2.wireOp",EDGE,"E44.sketch_text.stroke-0")}),-1.0]])]});
            var Q6;
            Q6=makeQuery(id+"F2.imprint","IMPRINT",FACE,{"disambiguationData":[TD([[makeQuery(id+"F2.imprint","IMPRINT",EDGE,{"derivedFrom":sQuery(id+"F2.wireOp",EDGE,"E45.sketch_text.stroke-0")}),-1.0]])]});
            var Q7;
            Q7=makeQuery(id+"F2.imprint","IMPRINT",FACE,{"disambiguationData":[TD([[makeQuery(id+"F2.imprint","IMPRINT",EDGE,{"derivedFrom":sQuery(id+"F2.wireOp",EDGE,"E45.sketch_text.stroke-8")}),-1.0]])]});
            extrude(context, id + "F3", {"entities" : qUnion([Q0, Q1, Q2, Q3, Q4, Q5, Q6, Q7]), "operationType" : NewBodyOperationType.ADD, "depth" : 1 * mm});
        }
    });
